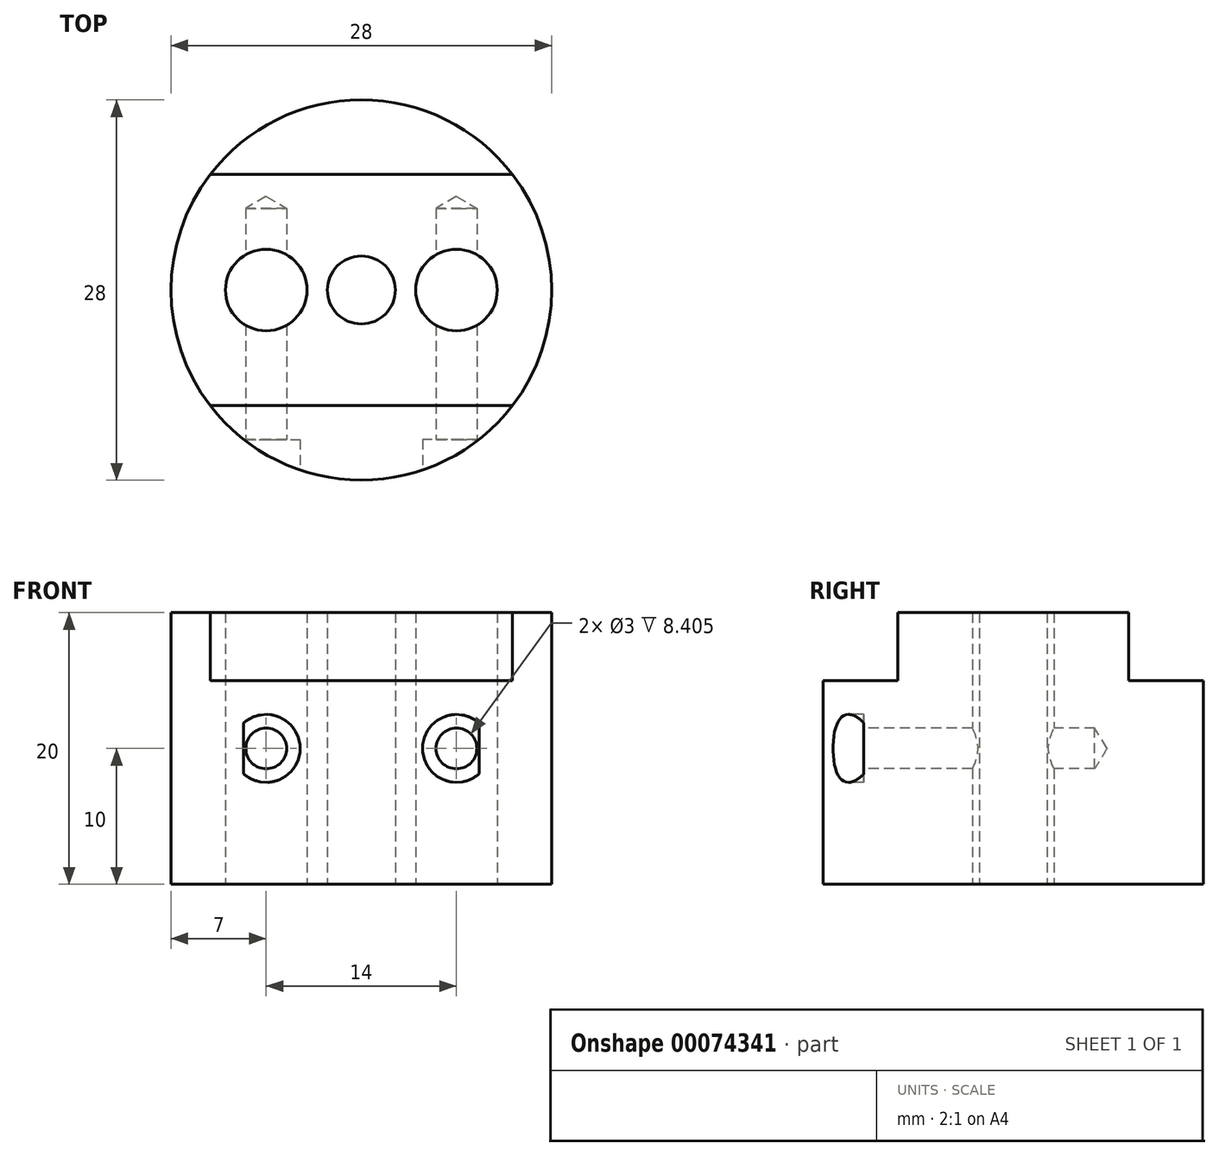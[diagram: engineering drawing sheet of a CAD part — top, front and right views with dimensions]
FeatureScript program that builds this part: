
annotation { "Feature Type Name" : "Feature", "Feature Type Description" : "" }
export const myFeature = defineFeature(function(context is Context, id is Id, definition is map)
    precondition{}
    {
        {
            var Q0;
            Q0=qCreatedBy(makeId("Top.planeOp"),FACE);
            var sketch = newSketch(context, id + "F0", { "sketchPlane" : qUnion([Q0])});
            skCircle(sketch, "E0", {"center": v(0, 0) * mm, "radius": 14 * mm});
            skCircle(sketch, "E1", {"center": v(0, 0) * mm, "radius": 3 * mm});
            skCircle(sketch, "E2", {"center": v(7, 0) * mm, "radius": 3 * mm});
            skCircle(sketch, "E3", {"center": v(-7, 0) * mm, "radius": 3 * mm});
            skCircle(sketch, "E4", {"center": v(0, 5) * mm, "radius": 1 * mm});
            skSolve(sketch);
        }
        {
            var Q0;
            Q0=makeQuery(id+"F0.imprint","IMPRINT",FACE,{"disambiguationData":[TD([[makeQuery(id+"F0.imprint","IMPRINT",EDGE,{"derivedFrom":sQuery(id+"F0.wireOp",EDGE,"E3")}),1.0]])]});
            var Q1;
            Q1=makeQuery(id+"F0.imprint","IMPRINT",FACE,{"disambiguationData":[TD([[makeQuery(id+"F0.imprint","IMPRINT",EDGE,{"derivedFrom":sQuery(id+"F0.wireOp",EDGE,"E0")}),1.0]])]});
            var Q2;
            Q2=makeQuery(id+"F0.imprint","IMPRINT",FACE,{"disambiguationData":[TD([[makeQuery(id+"F0.imprint","IMPRINT",EDGE,{"derivedFrom":sQuery(id+"F0.wireOp",EDGE,"E1")}),1.0]])]});
            var Q3;
            Q3=makeQuery(id+"F0.imprint","IMPRINT",FACE,{"disambiguationData":[TD([[makeQuery(id+"F0.imprint","IMPRINT",EDGE,{"derivedFrom":sQuery(id+"F0.wireOp",EDGE,"E2")}),1.0]])]});
            var Q4;
            Q4=makeQuery(id+"F0.imprint","IMPRINT",FACE,{"disambiguationData":[TD([[makeQuery(id+"F0.imprint","IMPRINT",EDGE,{"derivedFrom":sQuery(id+"F0.wireOp",EDGE,"E4")}),1.0]])]});
            extrude(context, id + "F1", {"entities" : qUnion([Q0, Q1, Q2, Q3, Q4]), "depth" : 20 * mm});
        }
        {
            var Q0;
            Q0=sQuery(id+"F0.wireOp",VERTEX,"E3.center");
            var Q1;
            Q1=sQuery(id+"F0.wireOp",VERTEX,"E2.center");
            var Q2;
            Q2=makeQuery(id+"F1.opExtrude","SWEPT_BODY",BODY,{"disambiguationData":[OSD([sQuery(id+"F0.wireOp",EDGE,"E0")])]});
            hole(context, id + "F2", {"style" : HoleStyle.SIMPLE, "endStyle" : HoleEndStyle.THROUGH, "oppositeDirection" : true, "holeDiameter" : 6 * mm, "startFromSketch" : true, "locations" : qUnion([Q0, Q1]), "scope" : qUnion([Q2]), "isTappedThrough" : true});
        }
        {
            var Q0;
            Q0=qCreatedBy(makeId("Front.planeOp"),FACE);
            cPlane(context, id + "F3", {"entities" : qUnion([Q0]), "cplaneType" : CPlaneType.OFFSET, "offset" : (28 / 2) * mm, "width" : 150 * mm, "height" : 150 * mm});
        }
        {
            var Q0;
            Q0=qCreatedBy(id+"F3.planeOp",FACE);
            var sketch = newSketch(context, id + "F4", { "sketchPlane" : qUnion([Q0])});
            skLineSegment(sketch, "E5", {"start": v(-14, 0) * mm, "end": v(-14, 20) * mm});
            skLineSegment(sketch, "E6", {"start": v(14, 20) * mm, "end": v(14, 0) * mm});
            skLineSegment(sketch, "E7.0", {"start": v(-10, 20) * mm, "end": v(-4, 20) * mm});
            skLineSegment(sketch, "E8.0", {"start": v(4, 20) * mm, "end": v(10, 20) * mm});
            skCircle(sketch, "E9", {"center": v(-7, 10) * mm, "radius": 1 * mm, "construction": true});
            skPoint(sketch, "E9.centerSnap0", {"position": v(-14, 10) * mm});
            skPoint(sketch, "E9.centerSnap1", {"position": v(-7, 20) * mm});
            skCircle(sketch, "E10", {"center": v(7, 10) * mm, "radius": 1 * mm, "construction": true});
            skPoint(sketch, "E10.centerSnap0", {"position": v(14, 10) * mm});
            skPoint(sketch, "E10.centerSnap1", {"position": v(7, 20) * mm});
            skSolve(sketch);
        }
        {
            var Q0;
            Q0=sQuery(id+"F4.wireOp",VERTEX,"E9.center");
            var Q1;
            Q1=sQuery(id+"F4.wireOp",VERTEX,"E10.center");
            var Q2;
            Q2=makeQuery(id+"F1.opExtrude","SWEPT_BODY",BODY,{"disambiguationData":[OSD([sQuery(id+"F0.wireOp",EDGE,"E0"),sQuery(id+"F0.wireOp",EDGE,"E1"),sQuery(id+"F0.wireOp",EDGE,"E2"),sQuery(id+"F0.wireOp",EDGE,"E3")])]});
            hole(context, id + "F5", {"style" : HoleStyle.C_BORE, "endStyle" : HoleEndStyle.BLIND, "holeDiameter" : 3 * mm, "cBoreDiameter" : 5 * mm, "cBoreDepth" : 3 * mm, "holeDepth" : 20 * mm, "startFromSketch" : true, "locations" : qUnion([Q0, Q1]), "scope" : qUnion([Q2])});
        }
        {
            var Q0;
            Q0=makeQuery(id+"F1.opExtrude","CAP_FACE",FACE,{"disambiguationData":[OSD([sQuery(id+"F0.wireOp",EDGE,"E0"),sQuery(id+"F0.wireOp",EDGE,"E1"),sQuery(id+"F0.wireOp",EDGE,"E2"),sQuery(id+"F0.wireOp",EDGE,"E3")])],"isStart":false});
            var sketch = newSketch(context, id + "F6", { "sketchPlane" : qUnion([Q0])});
            skLineSegment(sketch, "E11.bottom", {"start": v(11.12, 8.5) * mm, "end": v(-11.12, 8.5) * mm});
            skLineSegment(sketch, "E11.top", {"start": v(11.12, -8.5) * mm, "end": v(-11.12, -8.5) * mm});
            skLineSegment(sketch, "E11.left", {"start": v(11.12, 8.5) * mm, "end": v(11.12, -8.5) * mm});
            skLineSegment(sketch, "E11.right", {"start": v(-11.12, 8.5) * mm, "end": v(-11.12, -8.5) * mm});
            skSolve(sketch);
        }
        {
            var Q0;
            {var subQ0=sQuery(id+"F6.wireOp",EDGE,"E11.bottom");Q0=makeQuery(id+"F6.imprint","IMPRINT",FACE,{"disambiguationData":[TD([[makeQuery(id+"F6.imprint","IMPRINT",EDGE,{"derivedFrom":subQ0}),-1.0]])]});}
            var Q1;
            {var subQ0=sQuery(id+"F6.wireOp",EDGE,"E11.top");Q1=makeQuery(id+"F6.imprint","IMPRINT",FACE,{"disambiguationData":[TD([[makeQuery(id+"F6.imprint","IMPRINT",EDGE,{"derivedFrom":subQ0}),1.0]])]});}
            extrude(context, id + "F7", {"entities" : qUnion([Q0, Q1]), "operationType" : NewBodyOperationType.REMOVE, "oppositeDirection" : true, "depth" : 5 * mm});
        }
        {
            var Q0;
            Q0=sQuery(id+"F0.wireOp",VERTEX,"E0.center");
            var Q1;
            Q1=makeQuery(id+"F1.opExtrude","SWEPT_BODY",BODY,{"disambiguationData":[OSD([sQuery(id+"F0.wireOp",EDGE,"E0")])]});
            hole(context, id + "F8", {"style" : HoleStyle.SIMPLE, "endStyle" : HoleEndStyle.THROUGH, "oppositeDirection" : true, "standardTappedOrClearance" : lookupTablePath({ "standard" : "ISO", "engagement" : "75%", "pitch" : "1 mm", "size" : "M6", "type" : "Tapped" }), "standardBlindInLast" : lookupTablePath({ "standard" : "ISO", "engagement" : "75%", "pitch" : "1 mm", "size" : "M6", "type" : "Tapped" }), "holeDiameter" : 5 * mm, "startFromSketch" : true, "locations" : qUnion([Q0]), "scope" : qUnion([Q1]), "isTappedThrough" : true, "majorDiameter" : 6 * mm, "showTappedDepth" : true});
        }
    });
